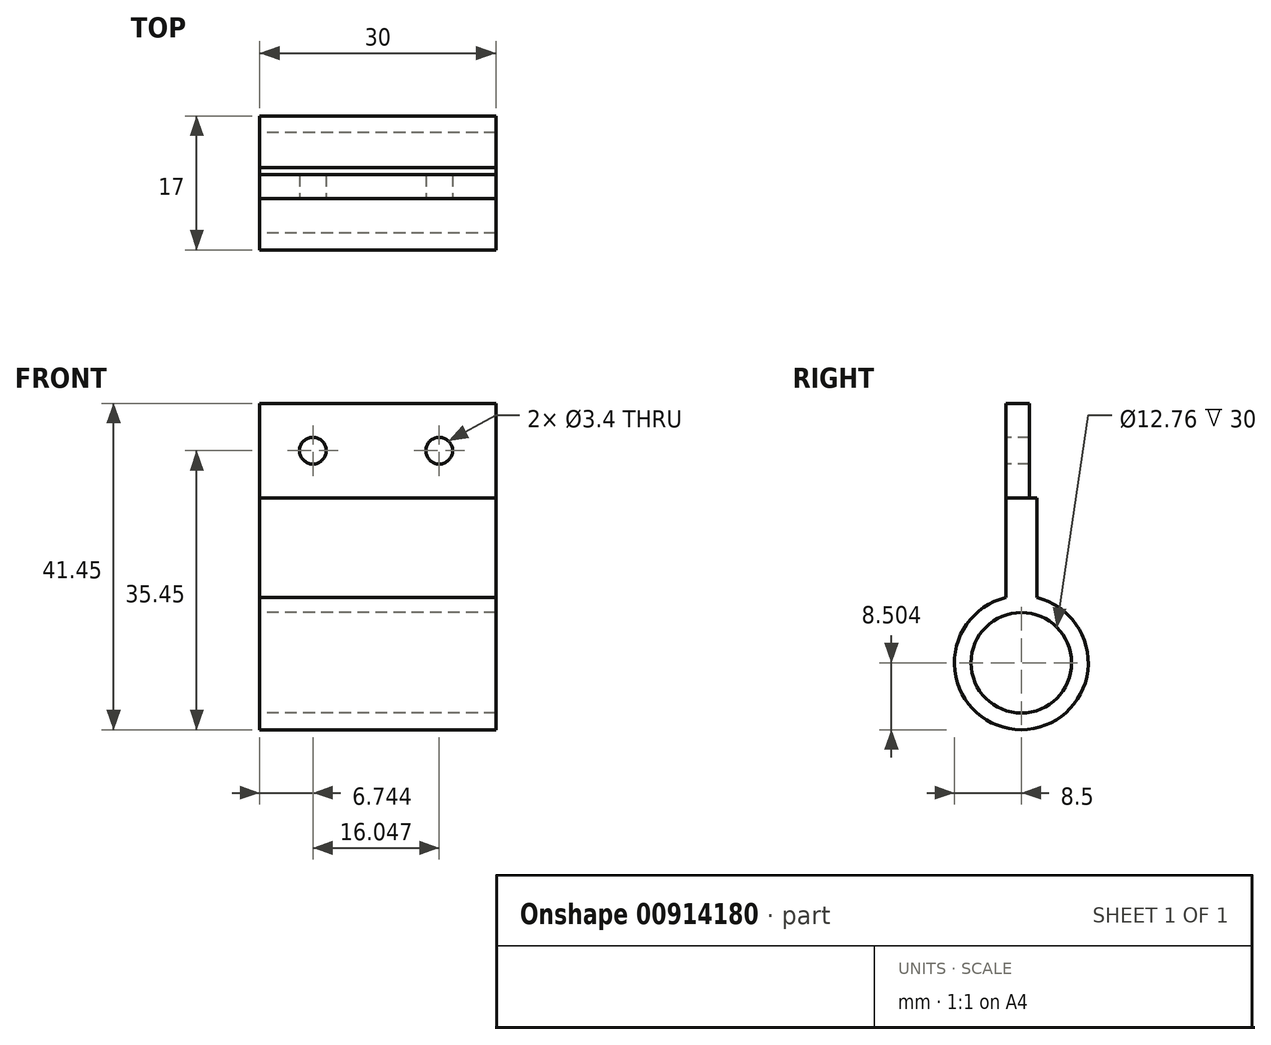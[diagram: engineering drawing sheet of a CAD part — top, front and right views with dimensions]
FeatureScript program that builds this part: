
annotation { "Feature Type Name" : "Feature", "Feature Type Description" : "" }
export const myFeature = defineFeature(function(context is Context, id is Id, definition is map)
    precondition{}
    {
        {
            var Q0;
            Q0=qCreatedBy(makeId("Front.planeOp"),FACE);
            var sketch = newSketch(context, id + "F0", { "sketchPlane" : qUnion([Q0])});
            skLineSegment(sketch, "E0.bottom", {"start": v(-15, -6) * mm, "end": v(15, -6) * mm});
            skLineSegment(sketch, "E0.top", {"start": v(-15, 6) * mm, "end": v(15, 6) * mm});
            skLineSegment(sketch, "E0.left", {"start": v(-15, -6) * mm, "end": v(-15, 6) * mm});
            skLineSegment(sketch, "E0.right", {"start": v(15, -6) * mm, "end": v(15, 6) * mm});
            skPoint(sketch, "E0.middle", {"position": v(0, 0) * mm});
            skCircle(sketch, "E1", {"center": v(7.8, 0) * mm, "radius": 1.7 * mm});
            skCircle(sketch, "E2", {"center": v(-8.26, 0) * mm, "radius": 1.7 * mm});
            skSolve(sketch);
        }
        {
            var Q0;
            Q0=makeQuery(id+"F0.imprint","IMPRINT",FACE,{"disambiguationData":[TD([[makeQuery(id+"F0.imprint","IMPRINT",EDGE,{"derivedFrom":sQuery(id+"F0.wireOp",EDGE,"E0.bottom")}),1.0]])]});
            extrude(context, id + "F1", {"entities" : qUnion([Q0]), "oppositeDirection" : true, "depth" : 3 * mm, "offsetDistance" : 25 * mm});
        }
        {
            var Q0;
            Q0=qCreatedBy(makeId("Front.planeOp"),FACE);
            var sketch = newSketch(context, id + "F2", { "sketchPlane" : qUnion([Q0])});
            skLineSegment(sketch, "E3.bottom", {"start": v(-15, -21) * mm, "end": v(15, -21) * mm});
            skLineSegment(sketch, "E3.top", {"start": v(-15, -6) * mm, "end": v(15, -6) * mm});
            skLineSegment(sketch, "E3.left", {"start": v(-15, -21) * mm, "end": v(-15, -6) * mm});
            skLineSegment(sketch, "E3.right", {"start": v(15, -21) * mm, "end": v(15, -6) * mm});
            skPoint(sketch, "E3.middle", {"position": v(0, -13.5) * mm});
            skSolve(sketch);
        }
        {
            var Q0;
            Q0=makeQuery(id+"F2.imprint","IMPRINT",FACE,{"disambiguationData":[TD([[makeQuery(id+"F2.imprint","IMPRINT",EDGE,{"derivedFrom":sQuery(id+"F2.wireOp",EDGE,"E3.bottom")}),1.0]])]});
            extrude(context, id + "F3", {"entities" : qUnion([Q0]), "oppositeDirection" : true, "depth" : 3.9 * mm, "offsetDistance" : 25 * mm});
        }
        {
            var Q0;
            Q0=makeQuery(id+"F3.opExtrude","SWEPT_FACE",FACE,{"disambiguationData":[OSD([sQuery(id+"F2.wireOp",EDGE,"E3.left")])]});
            var sketch = newSketch(context, id + "F4", { "sketchPlane" : qUnion([Q0])});
            skLineSegment(sketch, "E4", {"start": v(-1.95, -21) * mm, "end": v(-1.95, -41.1) * mm, "construction": true});
            skCircle(sketch, "E5", {"center": v(-1.95, -26.95) * mm, "radius": 8.5 * mm});
            skSolve(sketch);
        }
        {
            var Q0;
            {var subQ1=sQuery(id+"F2.wireOp",EDGE,"E3.left");var subQ6=makeQuery(id+"F3.opExtrude","SWEPT_EDGE",EDGE,{"disambiguationData":[OSD([sQuery(id+"F2.wireOp",EDGE,"E3.bottom"),subQ1])]});Q0=makeQuery(id+"F4.imprint","IMPRINT",FACE,{"disambiguationData":[TD([[makeQuery(id+"F4.imprint","IMPRINT",EDGE,{"derivedFrom":subQ6}),-1.0]])]});}
            extrude(context, id + "F5", {"entities" : qUnion([Q0]), "operationType" : NewBodyOperationType.ADD, "oppositeDirection" : true, "depth" : 30 * mm, "offsetDistance" : 25 * mm});
        }
        {
            var Q0;
            {var subQ0=sQuery(id+"F2.wireOp",EDGE,"E3.left");Q0=makeQuery(id+"F5.boolean.opBoolean","MERGE",FACE,{"derivedFrom":[makeQuery(id+"F3.opExtrude","SWEPT_FACE",FACE,{"disambiguationData":[OSD([subQ0])]}),makeQuery(id+"F5.opExtrude","CAP_FACE",FACE,{"disambiguationData":[OSD([sQuery(id+"F2.wireOp",EDGE,"E3.bottom"),subQ0,sQuery(id+"F4.wireOp",EDGE,"E5")])],"isStart":true})]});}
            var sketch = newSketch(context, id + "F6", { "sketchPlane" : qUnion([Q0])});
            skLineSegment(sketch, "E6", {"start": v(-1.95, -26.95) * mm, "end": v(-18.11, -26.95) * mm, "construction": true});
            skCircle(sketch, "E7", {"center": v(-1.95, -26.95) * mm, "radius": 6.38 * mm});
            skSolve(sketch);
        }
        {
            var Q0;
            Q0=makeQuery(id+"F6.imprint","IMPRINT",FACE,{"disambiguationData":[TD([[makeQuery(id+"F6.imprint","IMPRINT",EDGE,{"derivedFrom":sQuery(id+"F6.wireOp",EDGE,"E7")}),1.0]])]});
            extrude(context, id + "F7", {"entities" : qUnion([Q0]), "operationType" : NewBodyOperationType.REMOVE, "endBound" : BoundingType.THROUGH_ALL, "oppositeDirection" : true, "depth" : 25 * mm, "offsetDistance" : 25 * mm});
        }
    });
